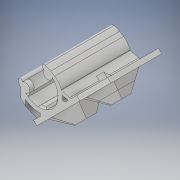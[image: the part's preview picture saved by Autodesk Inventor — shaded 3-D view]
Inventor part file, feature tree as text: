
AUTODESK INVENTOR PART (.ipt)
format: ipt  version: 2017 (Build 210142000, 142)  size: 1,037,824 bytes
history: native  units: in
note: dims shown in document units (in); Inventor stores cm internally (conversion verified against a paired STEP export)
features: other x2, extrude x2, sketch x2
ambient origin geometry x8: Origin, YZ Plane, XZ Plane, XY Plane, X Axis, Y Axis, Z Axis, Center Point
bodies: Solid1 (feature_tree)
feature tree (6):
  other  "10_Support plateau.STEP"
  extrude  "Extrusion1"  TaperAngle=0.0deg  [1 undecoded]
  extrude  "Extrusion3"  [1 undecoded]
  sketch  "Sketch1"  dims[d0=0.3937in d1=0.0in d4=0.0in d5=0.0in]
  sketch  "Sketch3"
  parser-record x1  (decoder bookkeeping rows leaked as tree rows — omitted from the tree; the rows remain in map.json)
note: 2 required parameter values undecoded (feature->parameter linkage not recoverable at this tier; creation-order binding heuristic only, values carry confidence <= 0.55)
